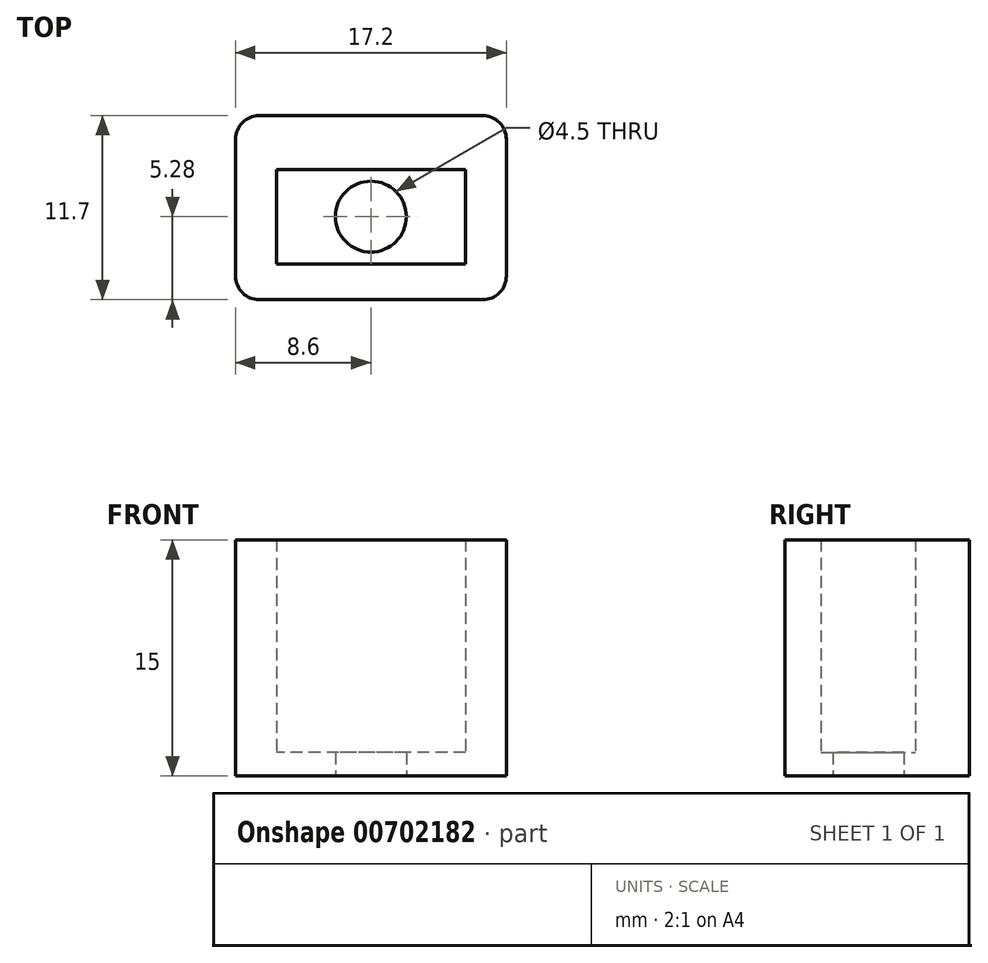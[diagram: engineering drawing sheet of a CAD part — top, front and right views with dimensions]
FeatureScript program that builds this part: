
annotation { "Feature Type Name" : "Feature", "Feature Type Description" : "" }
export const myFeature = defineFeature(function(context is Context, id is Id, definition is map)
    precondition{}
    {
        {
            var Q0;
            Q0=qCreatedBy(makeId("Top.planeOp"),FACE);
            var sketch = newSketch(context, id + "F0", { "sketchPlane" : qUnion([Q0])});
            skPoint(sketch, "E0.middle", {"position": v(0, 0) * mm});
            skPoint(sketch, "E1.middle", {"position": v(0, 3.26) * mm});
            skPoint(sketch, "E1.middle.positionSnap0", {"position": v(0, 2.5) * mm});
            skPoint(sketch, "E1.centerSnap0", {"position": v(0, 2.5) * mm});
            skLineSegment(sketch, "E2.bottom", {"start": v(8.6, -5.28) * mm, "end": v(-8.6, -5.28) * mm});
            skLineSegment(sketch, "E2.top", {"start": v(8.6, 6.42) * mm, "end": v(-8.6, 6.42) * mm});
            skLineSegment(sketch, "E2.left", {"start": v(8.6, -5.28) * mm, "end": v(8.6, 6.42) * mm});
            skLineSegment(sketch, "E2.right", {"start": v(-8.6, -5.28) * mm, "end": v(-8.6, 6.42) * mm});
            skPoint(sketch, "E2.middle", {"position": v(0, 0.57) * mm});
            skLineSegment(sketch, "E3.bottom", {"start": v(6, -3) * mm, "end": v(-6, -3) * mm});
            skLineSegment(sketch, "E3.top", {"start": v(6, 3) * mm, "end": v(-6, 3) * mm});
            skLineSegment(sketch, "E3.left", {"start": v(6, -3) * mm, "end": v(6, 3) * mm});
            skLineSegment(sketch, "E3.right", {"start": v(-6, -3) * mm, "end": v(-6, 3) * mm});
            skCircle(sketch, "E4", {"center": v(0, 0) * mm, "radius": 2.25 * mm});
            skSolve(sketch);
        }
        {
            var Q0;
            Q0=makeQuery(id+"F0.imprint","IMPRINT",FACE,{"disambiguationData":[TD([[makeQuery(id+"F0.imprint","IMPRINT",EDGE,{"derivedFrom":sQuery(id+"F0.wireOp",EDGE,"tryETO4A-KLSB-25rD-V5az-C2slfdcLXtNE.bottom")}),1.0]])]});
            var Q1;
            Q1=makeQuery(id+"F0.imprint","IMPRINT",FACE,{"disambiguationData":[TD([[makeQuery(id+"F0.imprint","IMPRINT",EDGE,{"derivedFrom":sQuery(id+"F0.wireOp",EDGE,"E2.bottom")}),-1.0]])]});
            extrude(context, id + "F1", {"entities" : qUnion([Q0, Q1]), "depth" : 15 * mm, "offsetDistance" : 25 * mm});
        }
        {
            var Q0;
            Q0=makeQuery(id+"F1.opExtrude","SWEPT_EDGE",EDGE,{"disambiguationData":[OSD([sQuery(id+"F0.wireOp",EDGE,"E2.top"),sQuery(id+"F0.wireOp",EDGE,"E2.right")])]});
            var Q1;
            Q1=makeQuery(id+"F1.opExtrude","SWEPT_EDGE",EDGE,{"disambiguationData":[OSD([sQuery(id+"F0.wireOp",EDGE,"E2.top"),sQuery(id+"F0.wireOp",EDGE,"E2.left")])]});
            var Q2;
            Q2=makeQuery(id+"F1.opExtrude","SWEPT_EDGE",EDGE,{"disambiguationData":[OSD([sQuery(id+"F0.wireOp",EDGE,"E2.bottom"),sQuery(id+"F0.wireOp",EDGE,"E2.left")])]});
            var Q3;
            Q3=makeQuery(id+"F1.opExtrude","SWEPT_EDGE",EDGE,{"disambiguationData":[OSD([sQuery(id+"F0.wireOp",EDGE,"E2.bottom"),sQuery(id+"F0.wireOp",EDGE,"E2.right")])]});
            fillet(context, id + "F2", {"entities" : qUnion([Q0, Q1, Q2, Q3]), "radius" : 1.5 * mm, "tangentPropagation" : true, "allowEdgeOverflow" : false});
        }
        {
            var Q0;
            {var subQ0=sQuery(id+"F0.wireOp",EDGE,"E3.left");Q0=makeQuery(id+"F0.imprint","IMPRINT",FACE,{"disambiguationData":[TD([[makeQuery(id+"F0.imprint","IMPRINT",EDGE,{"derivedFrom":subQ0}),1.0]])]});}
            var Q1;
            {var subQ0=sQuery(id+"F0.wireOp",EDGE,"E3.right");Q1=makeQuery(id+"F0.imprint","IMPRINT",FACE,{"disambiguationData":[TD([[makeQuery(id+"F0.imprint","IMPRINT",EDGE,{"derivedFrom":subQ0}),-1.0]])]});}
            extrude(context, id + "F3", {"entities" : qUnion([Q0, Q1]), "operationType" : NewBodyOperationType.ADD, "depth" : 1.5 * mm, "offsetDistance" : 25 * mm});
        }
    });
